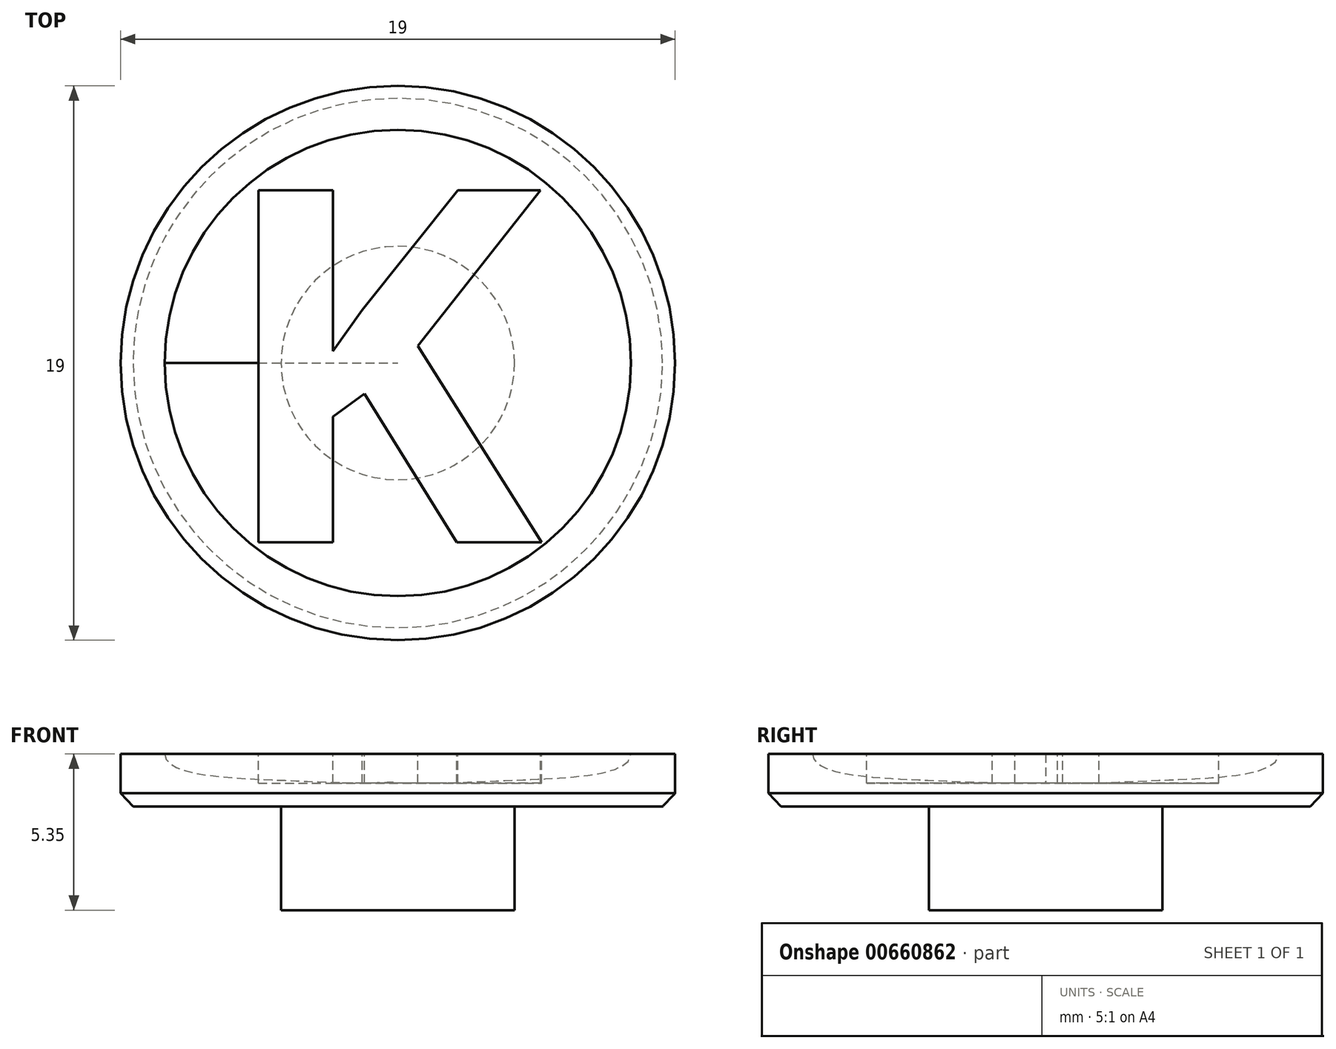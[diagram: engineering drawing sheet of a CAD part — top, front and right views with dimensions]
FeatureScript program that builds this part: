
annotation { "Feature Type Name" : "Feature", "Feature Type Description" : "" }
export const myFeature = defineFeature(function(context is Context, id is Id, definition is map)
    precondition{}
    {
        {
            var Q0;
            Q0=qCreatedBy(makeId("Front.planeOp"),FACE);
            var sketch = newSketch(context, id + "F0", { "sketchPlane" : qUnion([Q0])});
            skLineSegment(sketch, "E0", {"start": v(-9.5, 1.8) * mm, "end": v(-8, 1.8) * mm});
            skLineSegment(sketch, "E1", {"start": v(-9.5, 1.8) * mm, "end": v(-9.5, 0.45) * mm});
            skLineSegment(sketch, "E2", {"start": v(-9.07, 0) * mm, "end": v(0, 0) * mm});
            skLineSegment(sketch, "E3", {"start": v(-9.5, 0.45) * mm, "end": v(-9.07, 0) * mm});
            skFitSpline(sketch, "E4", {"points": [v(-8, 1.8) * mm, v(-4.15, 0.9) * mm, v(0, 0.85) * mm], "startDerivative": vector(0, -4.6) * mm, "endDerivative": vector(8.52, 0.54) * mm});
            skLineSegment(sketch, "E5", {"start": v(0, 0) * mm, "end": v(0, 0.85) * mm});
            skLineSegment(sketch, "E6", {"start": v(0, 2.4) * mm, "end": v(0, 0) * mm, "construction": true});
            skSolve(sketch);
        }
        {
            var Q0;
            Q0=qSketchRegion(id+"F0",true);
            var Q1;
            Q1=sQuery(id+"F0.wireOp",EDGE,"E6");
            revolve(context, id + "F1", {"entities" : qUnion([Q0]), "axis" : qUnion([Q1]), "revolveType" : RevolveType.FULL});
        }
        {
            var Q0;
            Q0=makeQuery(id+"F1.opRevolve","SWEPT_FACE",FACE,{"disambiguationData":[OSD([sQuery(id+"F0.wireOp",EDGE,"E2")])]});
            var sketch = newSketch(context, id + "F2", { "sketchPlane" : qUnion([Q0])});
            skCircle(sketch, "E7", {"center": v(0, 0) * mm, "radius": 4 * mm});
            skSolve(sketch);
        }
        {
            var Q0;
            Q0=makeQuery(id+"F2.imprint","IMPRINT",FACE,{"disambiguationData":[TD([[makeQuery(id+"F2.imprint","IMPRINT",EDGE,{"derivedFrom":sQuery(id+"F2.wireOp",EDGE,"E7")}),1.0]])]});
            extrude(context, id + "F3", {"entities" : qUnion([Q0]), "operationType" : NewBodyOperationType.ADD, "depth" : 3.55 * mm, "offsetDistance" : 25 * mm});
        }
        {
            var Q0;
            Q0=makeQuery(id+"F1.opRevolve","SWEPT_FACE",FACE,{"disambiguationData":[OSD([sQuery(id+"F0.wireOp",EDGE,"E0")])]});
            var sketch = newSketch(context, id + "F4", { "sketchPlane" : qUnion([Q0])});
            skText(sketch, "E8", { "text": "K", "fontName": "OpenSans-Bold.ttf"});
            const initialGuessF4  = {"E8": [-0.0063, -0.00614, 1, 0, 0.01217]};
            skSetInitialGuess(sketch, initialGuessF4);
            skSolve(sketch);
        }
        {
            var Q0;
            Q0 = qSketchRegion(id + "F4", true);
            extrude(context, id + "F5", {"entities" : qUnion([Q0]), "oppositeDirection" : true, "depth" : 1 * mm, "offsetDistance" : 25 * mm});
        }
    });
